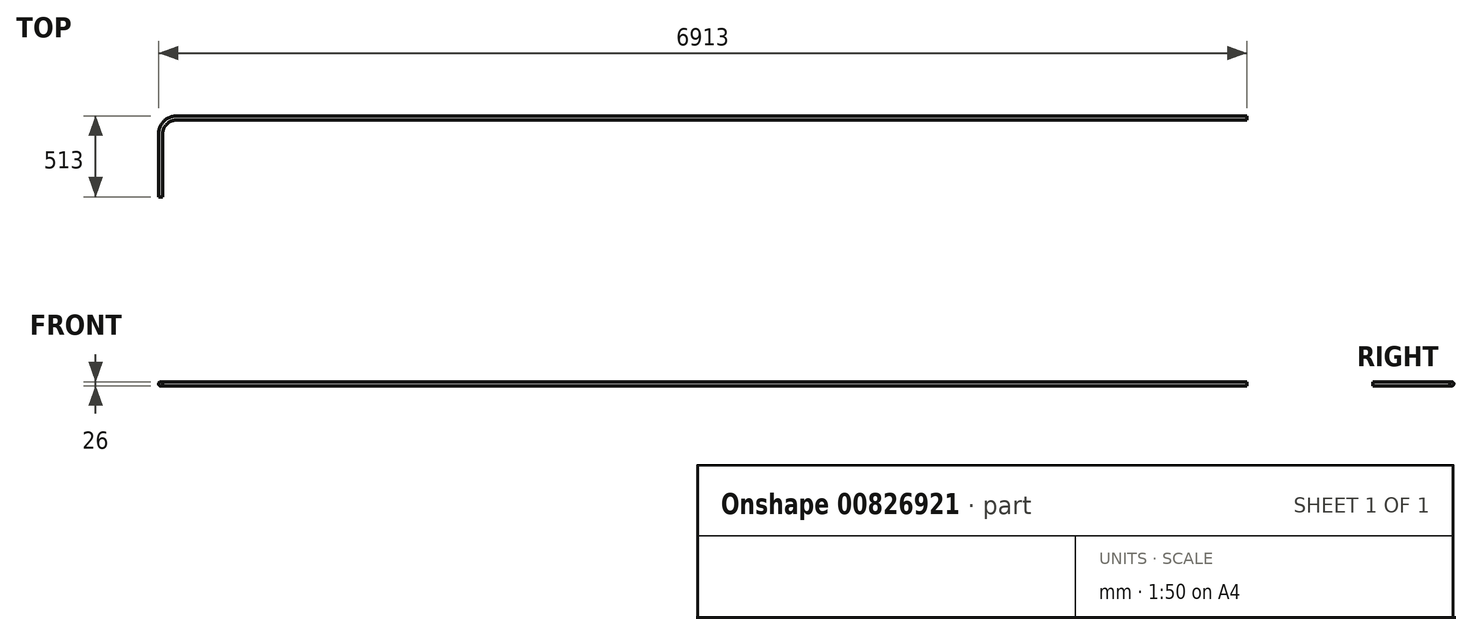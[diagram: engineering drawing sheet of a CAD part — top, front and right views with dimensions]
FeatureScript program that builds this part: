
annotation { "Feature Type Name" : "Feature", "Feature Type Description" : "" }
export const myFeature = defineFeature(function(context is Context, id is Id, definition is map)
    precondition{}
    {
        {
            var Q0;
            Q0=qCreatedBy(makeId("Top.planeOp"),FACE);
            var sketch = newSketch(context, id + "F0", { "sketchPlane" : qUnion([Q0])});
            skLineSegment(sketch, "E0", {"start": v(0, 0) * mm, "end": v(0, 400) * mm});
            skLineSegment(sketch, "E1", {"start": v(100, 500) * mm, "end": v(6900, 500) * mm});
            skPoint(sketch, "E2.visualSharp", {"position": v(0, 500) * mm});
            skArc(sketch, "E2.filletArc", {"start": v(100, 500) * mm, "mid": v(29.29, 470.71) * mm, "end": v(0, 400) * mm});
            skSolve(sketch);
        }
        {
            var Q0;
            Q0=qCreatedBy(makeId("Front.planeOp"),FACE);
            var sketch = newSketch(context, id + "F1", { "sketchPlane" : qUnion([Q0])});
            skCircle(sketch, "E3", {"center": v(0, 0) * mm, "radius": 13 * mm});
            skSolve(sketch);
        }
        {
            var Q0;
            Q0=makeQuery(id+"F1.imprint","IMPRINT",FACE,{"disambiguationData":[TD([[makeQuery(id+"F1.imprint","IMPRINT",EDGE,{"derivedFrom":sQuery(id+"F1.wireOp",EDGE,"E3")}),1.0]])]});
            var Q1;
            Q1=sQuery(id+"F0.wireOp",EDGE,"E0");
            var Q2;
            Q2=sQuery(id+"F0.wireOp",EDGE,"E2.filletArc");
            var Q3;
            Q3=sQuery(id+"F0.wireOp",EDGE,"E1");
            var Q4;
            Q4=sQuery(id+"F0.wireOp",EDGE,"4d499999-df77-4b60-a4ba-897b6893fd93.filletArc");
            var Q5;
            Q5=sQuery(id+"F0.wireOp",EDGE,"8WITOyXH-THkU-0kex-jkAY-4B5OXCUn6dDO");
            var Q6;
            Q6=sQuery(id+"F0.wireOp",EDGE,"aff54f4b-6d01-47bc-8007-841d74a99995.filletArc");
            var Q7;
            Q7=sQuery(id+"F0.wireOp",EDGE,"YWYMzJ76-O9c7-8fMm-sKql-zo2dPW1WVBY2");
            sweep(context, id + "F2", {"profiles" : qUnion([Q0]), "path" : qUnion([Q1, Q2, Q3, Q4, Q5, Q6, Q7])});
        }
    });
